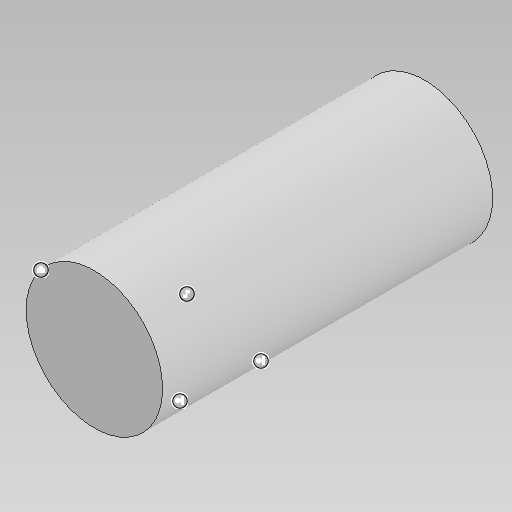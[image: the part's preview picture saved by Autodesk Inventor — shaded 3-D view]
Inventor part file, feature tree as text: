
AUTODESK INVENTOR PART (.ipt)
format: ipt  version: 2020 (Build 240168000, 168)  size: 100,352 bytes
history: native  units: mm
features: extrude x1, sketch x1
ambient origin geometry x8: Origin, YZ Plane, XZ Plane, XY Plane, X Axis, Y Axis, Z Axis, Center Point
bodies: Solid1 (feature_tree)
feature tree (2):
  extrude  "Extrusion1"  TaperAngle=0.0deg  [1 undecoded]
  sketch  "Sketch1"  dims[d2=0.0mm d3=0.0mm d4=0.0mm d9=0.0mm d10=0.0mm]
note: 1 required parameter value undecoded (feature->parameter linkage not recoverable at this tier; creation-order binding heuristic only, values carry confidence <= 0.55)
